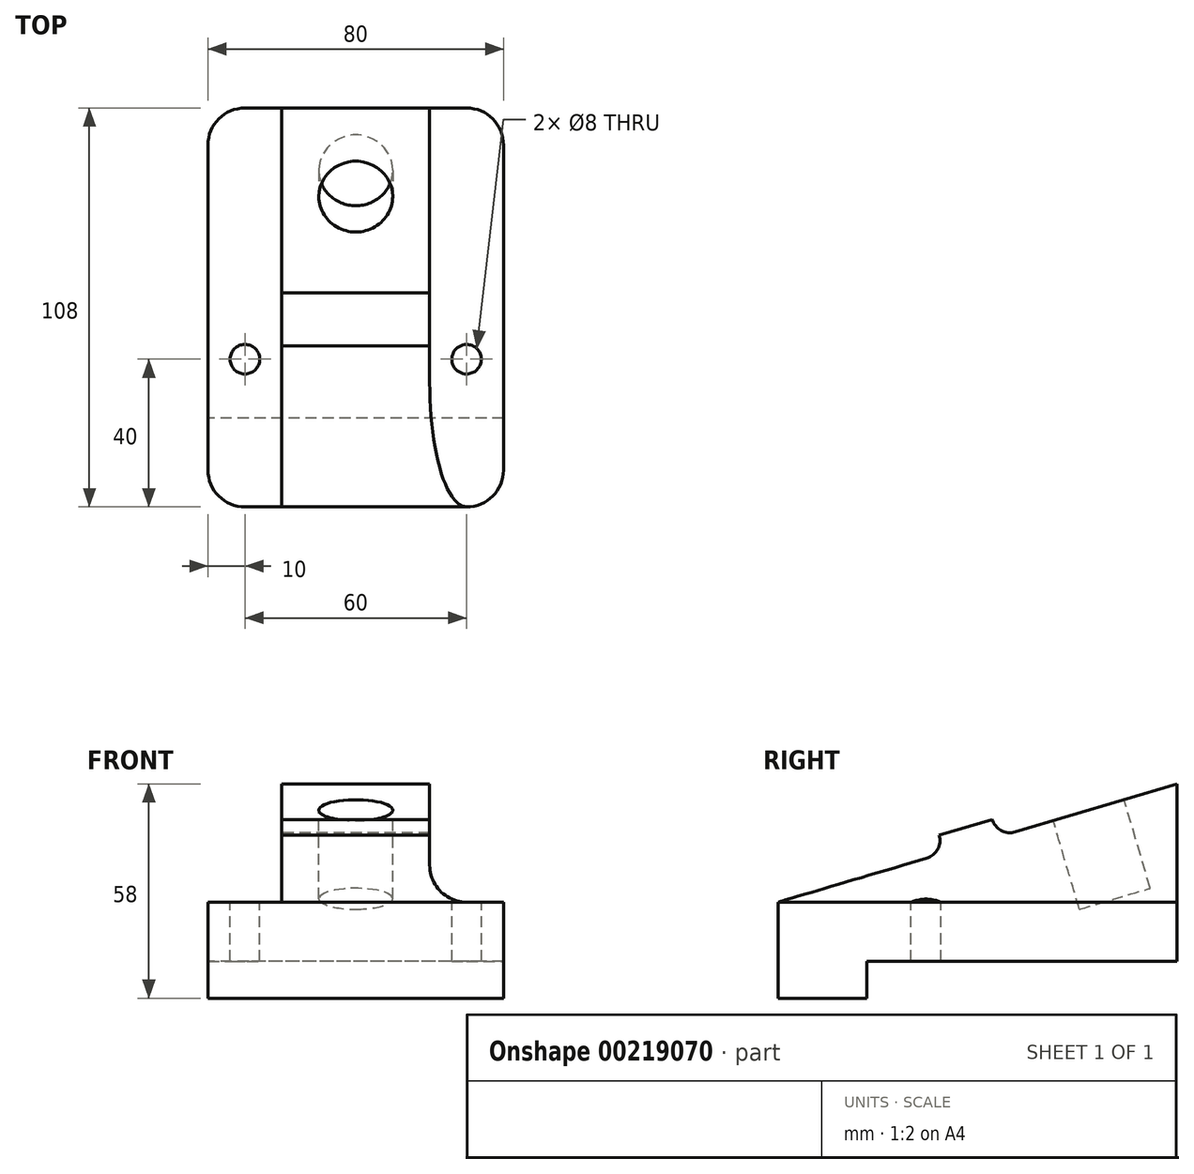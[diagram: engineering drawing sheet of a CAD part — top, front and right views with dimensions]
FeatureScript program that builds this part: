
annotation { "Feature Type Name" : "Feature", "Feature Type Description" : "" }
export const myFeature = defineFeature(function(context is Context, id is Id, definition is map)
    precondition{}
    {
        {
            var Q0;
            Q0=qCreatedBy(makeId("Right.planeOp"),FACE);
            var sketch = newSketch(context, id + "F0", { "sketchPlane" : qUnion([Q0])});
            skLineSegment(sketch, "E0.bottom", {"start": v(0, 0) * mm, "end": v(24, 0) * mm});
            skLineSegment(sketch, "E0.top", {"start": v(0, 26) * mm, "end": v(108, 26) * mm});
            skLineSegment(sketch, "E0.left", {"start": v(0, 0) * mm, "end": v(0, 26) * mm});
            skLineSegment(sketch, "E0.right", {"start": v(108, 10) * mm, "end": v(108, 26) * mm});
            skLineSegment(sketch, "E1", {"start": v(0, 26) * mm, "end": v(40.2, 37.91) * mm});
            skLineSegment(sketch, "E2", {"start": v(43.58, 44.13) * mm, "end": v(43.58, 44.13) * mm});
            skLineSegment(sketch, "E3", {"start": v(43.58, 44.13) * mm, "end": v(57.96, 48.39) * mm});
            skLineSegment(sketch, "E4", {"start": v(57.96, 48.39) * mm, "end": v(57.96, 48.39) * mm});
            skLineSegment(sketch, "E5", {"start": v(64.18, 45.02) * mm, "end": v(108, 58) * mm});
            skLineSegment(sketch, "E6", {"start": v(108, 58) * mm, "end": v(108, 26) * mm});
            skLineSegment(sketch, "E7", {"start": v(108, 10) * mm, "end": v(24, 10) * mm});
            skLineSegment(sketch, "E8", {"start": v(24, 10) * mm, "end": v(24, 0) * mm});
            skPoint(sketch, "E9.visualSharp", {"position": v(59.38, 43.6) * mm});
            skArc(sketch, "E9.filletArc", {"start": v(57.96, 48.39) * mm, "mid": v(60.37, 45.41) * mm, "end": v(64.18, 45.02) * mm});
            skPoint(sketch, "E10.visualSharp", {"position": v(45, 39.33) * mm});
            skArc(sketch, "E10.filletArc", {"start": v(40.2, 37.91) * mm, "mid": v(43.18, 40.32) * mm, "end": v(43.58, 44.13) * mm});
            skSolve(sketch);
        }
        {
            var Q0;
            Q0=makeQuery(id+"F0.imprint","IMPRINT",FACE,{"disambiguationData":[TD([[makeQuery(id+"F0.imprint","IMPRINT",EDGE,{"derivedFrom":sQuery(id+"F0.wireOp",EDGE,"E0.top")}),1.0]])]});
            extrude(context, id + "F1", {"entities" : qUnion([Q0]), "endBound" : BoundingType.SYMMETRIC, "depth" : 40 * mm});
        }
        {
            var Q0;
            Q0=makeQuery(id+"F0.imprint","IMPRINT",FACE,{"disambiguationData":[TD([[makeQuery(id+"F0.imprint","IMPRINT",EDGE,{"derivedFrom":sQuery(id+"F0.wireOp",EDGE,"E0.bottom")}),1.0]])]});
            extrude(context, id + "F2", {"entities" : qUnion([Q0]), "operationType" : NewBodyOperationType.ADD, "endBound" : BoundingType.SYMMETRIC, "depth" : 80 * mm});
        }
        {
            var Q0;
            Q0=makeQuery(id+"F2.opExtrude","CAP_EDGE",EDGE,{"disambiguationData":[OSD([sQuery(id+"F0.wireOp",EDGE,"E0.left")])],"isStart":false});
            var Q1;
            Q1=makeQuery(id+"F2.opExtrude","CAP_EDGE",EDGE,{"disambiguationData":[OSD([sQuery(id+"F0.wireOp",EDGE,"E0.right")])],"isStart":false});
            var Q2;
            Q2=makeQuery(id+"F2.opExtrude","CAP_EDGE",EDGE,{"disambiguationData":[OSD([sQuery(id+"F0.wireOp",EDGE,"E0.left")])],"isStart":true});
            var Q3;
            Q3=makeQuery(id+"F2.opExtrude","CAP_EDGE",EDGE,{"disambiguationData":[OSD([sQuery(id+"F0.wireOp",EDGE,"E0.right")])],"isStart":true});
            var Q4;
            Q4=makeQuery(id+"F1.opExtrude","CAP_EDGE",EDGE,{"disambiguationData":[OSD([sQuery(id+"F0.wireOp",EDGE,"E0.top")])],"isStart":false});
            var Q5;
            Q5=makeQuery(id+"F1.opExtrude","CAP_EDGE",EDGE,{"disambiguationData":[OSD([sQuery(id+"F0.wireOp",EDGE,"E0.top")])],"isStart":true});
            fillet(context, id + "F3", {"entities" : qUnion([Q0, Q1, Q2, Q3, Q4, Q5]), "radius" : 10 * mm, "tangentPropagation" : true, "allowEdgeOverflow" : false});
        }
        {
            var Q0;
            Q0=makeQuery(id+"F1.opExtrude","SWEPT_FACE",FACE,{"disambiguationData":[OSD([sQuery(id+"F0.wireOp",EDGE,"E5")])]});
            var sketch = newSketch(context, id + "F4", { "sketchPlane" : qUnion([Q0])});
            skCircle(sketch, "E11", {"center": v(0, 95.03) * mm, "radius": 10 * mm});
            skSolve(sketch);
        }
        {
            var Q0;
            Q0=makeQuery(id+"F4.imprint","IMPRINT",FACE,{"disambiguationData":[TD([[makeQuery(id+"F4.imprint","IMPRINT",EDGE,{"derivedFrom":sQuery(id+"F4.wireOp",EDGE,"E11")}),1.0]])]});
            extrude(context, id + "F5", {"entities" : qUnion([Q0]), "operationType" : NewBodyOperationType.REMOVE, "oppositeDirection" : true, "depth" : 25 * mm});
        }
        {
            var Q0;
            {var subQ0=sQuery(id+"F0.wireOp",EDGE,"E0.right");var subQ1=sQuery(id+"F0.wireOp",EDGE,"E0.left");var subQ2=sQuery(id+"F0.wireOp",EDGE,"E0.top");Q0=makeQuery(id+"F2.boolean.opBoolean","SPLIT",FACE,{"disambiguationData":[TD([makeQuery(id+"F2.opExtrude","CAP_FACE",FACE,{"disambiguationData":[OSD([sQuery(id+"F0.wireOp",EDGE,"E0.bottom"),subQ2,subQ1,subQ0,sQuery(id+"F0.wireOp",EDGE,"E7"),sQuery(id+"F0.wireOp",EDGE,"E8")])],"isStart":false})])],"derivedFrom":makeQuery(id+"F2.opExtrude","SWEPT_FACE",FACE,{"disambiguationData":[OSD([subQ2])]})});}
            var sketch = newSketch(context, id + "F6", { "sketchPlane" : qUnion([Q0])});
            skCircle(sketch, "E12", {"center": v(30, 40) * mm, "radius": 4 * mm});
            skCircle(sketch, "E13.MirrorC", {"center": v(-30, 40) * mm, "radius": 4 * mm});
            skSolve(sketch);
        }
        {
            var Q0;
            Q0 = qSketchRegion(id + "F6", true);
            extrude(context, id + "F7", {"entities" : qUnion([Q0]), "operationType" : NewBodyOperationType.REMOVE, "endBound" : BoundingType.UP_TO_NEXT, "oppositeDirection" : true, "depth" : 25 * mm});
        }
        {
            var Q0;
            Q0 = qSketchRegion(id + "F6", true);
            extrude(context, id + "F8", {"entities" : qUnion([Q0]), "operationType" : NewBodyOperationType.REMOVE, "depth" : 25 * mm});
        }
    });
